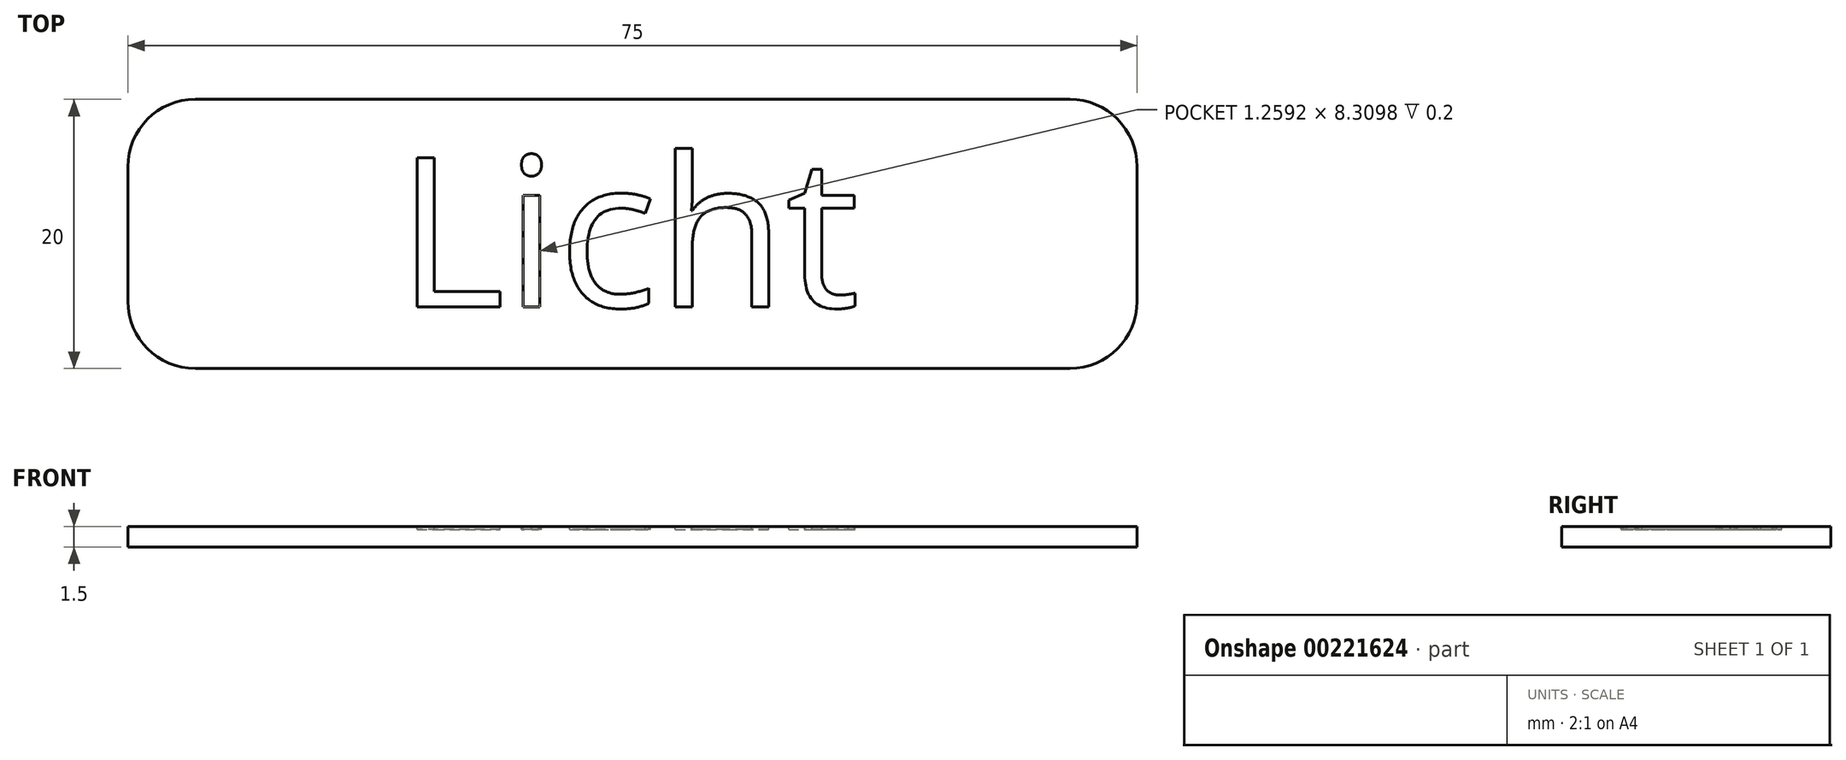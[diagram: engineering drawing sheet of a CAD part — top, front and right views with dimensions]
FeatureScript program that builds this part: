
annotation { "Feature Type Name" : "Feature", "Feature Type Description" : "" }
export const myFeature = defineFeature(function(context is Context, id is Id, definition is map)
    precondition{}
    {
        {
            var Q0;
            Q0=qCreatedBy(makeId("Top.planeOp"),FACE);
            var sketch = newSketch(context, id + "F0", { "sketchPlane" : qUnion([Q0])});
            skLineSegment(sketch, "E0.bottom", {"start": v(32.5, 10) * mm, "end": v(-32.5, 10) * mm});
            skLineSegment(sketch, "E0.top", {"start": v(32.5, -10) * mm, "end": v(-32.5, -10) * mm});
            skLineSegment(sketch, "E0.left", {"start": v(37.5, 5) * mm, "end": v(37.5, -5) * mm});
            skLineSegment(sketch, "E0.right", {"start": v(-37.5, 5) * mm, "end": v(-37.5, -5) * mm});
            skPoint(sketch, "E0.middle", {"position": v(0, 0) * mm});
            skPoint(sketch, "E1.visualSharp", {"position": v(-37.5, 10) * mm});
            skArc(sketch, "E1.filletArc", {"start": v(-32.5, 10) * mm, "mid": v(-36.04, 8.54) * mm, "end": v(-37.5, 5) * mm});
            skPoint(sketch, "E2.visualSharp", {"position": v(-37.5, -10) * mm});
            skArc(sketch, "E2.filletArc", {"start": v(-37.5, -5) * mm, "mid": v(-36.04, -8.54) * mm, "end": v(-32.5, -10) * mm});
            skPoint(sketch, "E3.visualSharp", {"position": v(37.5, -10) * mm});
            skArc(sketch, "E3.filletArc", {"start": v(32.5, -10) * mm, "mid": v(36.04, -8.54) * mm, "end": v(37.5, -5) * mm});
            skPoint(sketch, "E4.visualSharp", {"position": v(37.5, 10) * mm});
            skArc(sketch, "E4.filletArc", {"start": v(37.5, 5) * mm, "mid": v(36.04, 8.54) * mm, "end": v(32.5, 10) * mm});
            skSolve(sketch);
        }
        {
            var Q0;
            Q0=makeQuery(id+"F0.imprint","IMPRINT",FACE,{"disambiguationData":[TD([[makeQuery(id+"F0.imprint","IMPRINT",EDGE,{"derivedFrom":sQuery(id+"F0.wireOp",EDGE,"E0.bottom")}),1.0]])]});
            extrude(context, id + "F1", {"entities" : qUnion([Q0]), "depth" : 1.5 * mm, "offsetDistance" : 25 * mm});
        }
        {
            var Q0;
            Q0=makeQuery(id+"F1.opExtrude","CAP_FACE",FACE,{"disambiguationData":[OSD([sQuery(id+"F0.wireOp",EDGE,"E0.bottom"),sQuery(id+"F0.wireOp",EDGE,"E0.top"),sQuery(id+"F0.wireOp",EDGE,"E0.left"),sQuery(id+"F0.wireOp",EDGE,"E0.right"),sQuery(id+"F0.wireOp",EDGE,"E1.filletArc"),sQuery(id+"F0.wireOp",EDGE,"E2.filletArc"),sQuery(id+"F0.wireOp",EDGE,"E3.filletArc"),sQuery(id+"F0.wireOp",EDGE,"E4.filletArc")])],"isStart":false});
            var sketch = newSketch(context, id + "F2", { "sketchPlane" : qUnion([Q0])});
            skText(sketch, "E5", { "text": "Licht", "fontName": "OpenSans-Regular.ttf"});
            const initialGuessF2  = {"E5": [-0.01754, -0.00543, 1, 0, 0.01118]};
            skSetInitialGuess(sketch, initialGuessF2);
            skSolve(sketch);
        }
        {
            var Q0;
            Q0 = qSketchRegion(id + "F2", true);
            extrude(context, id + "F3", {"entities" : qUnion([Q0]), "operationType" : NewBodyOperationType.REMOVE, "oppositeDirection" : true, "depth" : 0.2 * mm, "offsetDistance" : 25 * mm});
        }
    });
